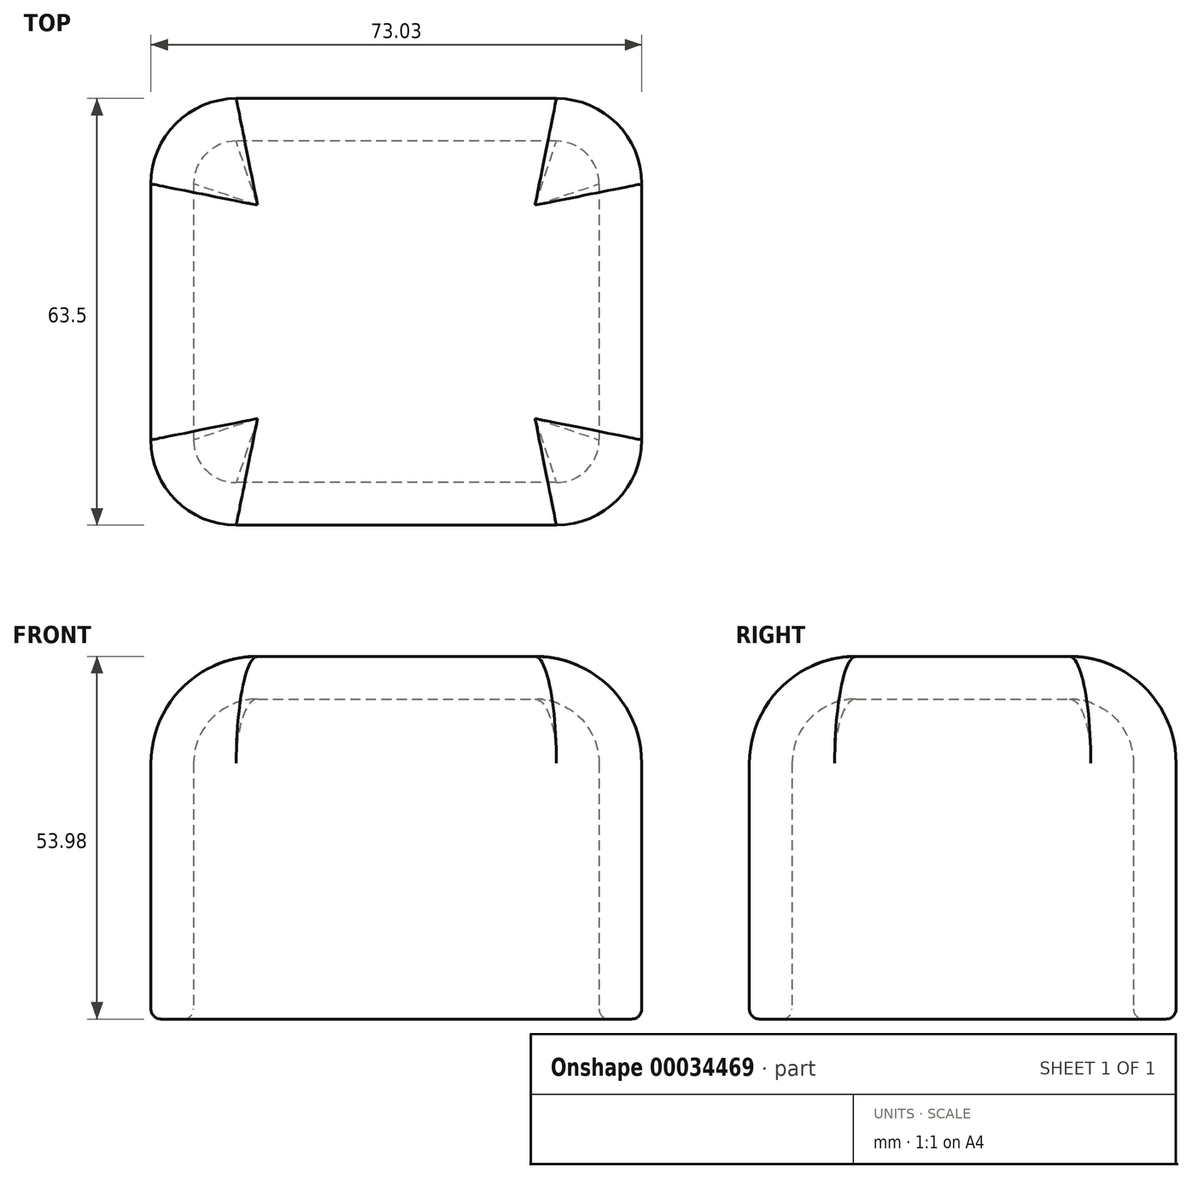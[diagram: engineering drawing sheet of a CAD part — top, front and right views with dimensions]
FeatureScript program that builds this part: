
annotation { "Feature Type Name" : "Feature", "Feature Type Description" : "" }
export const myFeature = defineFeature(function(context is Context, id is Id, definition is map)
    precondition{}
    {
        {
            var Q0;
            Q0=qCreatedBy(makeId("Top.planeOp"),FACE);
            var sketch = newSketch(context, id + "F4", { "sketchPlane" : qUnion([Q0])});
            skLineSegment(sketch, "E0.bottom", {"start": v(73.02, 63.5) * mm, "end": v(0, 63.5) * mm});
            skLineSegment(sketch, "E0.top", {"start": v(73.03, 0) * mm, "end": v(0, 0) * mm});
            skLineSegment(sketch, "E0.left", {"start": v(73.03, 63.5) * mm, "end": v(73.03, 0) * mm});
            skLineSegment(sketch, "E0.right", {"start": v(0, 63.5) * mm, "end": v(0, 0) * mm});
            skSolve(sketch);
        }
        {
            var Q0;
            Q0 = qSketchRegion(id + "F4", true);
            var sketch = newSketch(context, id + "F0", { "sketchPlane" : qUnion([Q0])});
            skSolve(sketch);
        }
        {
            var Q0;
            Q0 = qSketchRegion(id + "F0", true);
            var Q1;
            Q1=makeQuery(id+"F4.imprint","IMPRINT",FACE,{"disambiguationData":[TD([[makeQuery(id+"F4.imprint","IMPRINT",EDGE,{"derivedFrom":sQuery(id+"F4.wireOp",EDGE,"E0.bottom")}),1.0]])]});
            extrude(context, id + "F5", {"entities" : qUnion([Q0, Q1]), "depth" : 53.97 * mm});
        }
        {
            var Q0;
            Q0=makeQuery(id+"F5.opExtrude","SWEPT_EDGE",EDGE,{"disambiguationData":[OSD([sQuery(id+"F4.wireOp",EDGE,"E0.top"),sQuery(id+"F4.wireOp",EDGE,"E0.left")])]});
            var Q1;
            Q1=makeQuery(id+"F5.opExtrude","SWEPT_EDGE",EDGE,{"disambiguationData":[OSD([sQuery(id+"F4.wireOp",EDGE,"E0.bottom"),sQuery(id+"F4.wireOp",EDGE,"E0.left")])]});
            var Q2;
            Q2=makeQuery(id+"F5.opExtrude","SWEPT_EDGE",EDGE,{"disambiguationData":[OSD([sQuery(id+"F4.wireOp",EDGE,"E0.top"),sQuery(id+"F4.wireOp",EDGE,"E0.right")])]});
            var Q3;
            Q3=makeQuery(id+"F5.opExtrude","SWEPT_EDGE",EDGE,{"disambiguationData":[OSD([sQuery(id+"F4.wireOp",EDGE,"E0.bottom"),sQuery(id+"F4.wireOp",EDGE,"E0.right")])]});
            fillet(context, id + "F1", {"entities" : qUnion([Q0, Q1, Q2, Q3]), "radius" : 12.7 * mm, "tangentPropagation" : true, "allowEdgeOverflow" : false});
        }
        {
            var Q0;
            Q0=makeQuery(id+"F5.opExtrude","CAP_EDGE",EDGE,{"disambiguationData":[OSD([sQuery(id+"F4.wireOp",EDGE,"E0.right")])],"isStart":false});
            fillet(context, id + "F2", {"entities" : qUnion([Q0]), "radius" : 15.88 * mm, "tangentPropagation" : true, "allowEdgeOverflow" : false});
        }
        {
            var Q0;
            Q0=makeQuery(id+"F5.opExtrude","CAP_FACE",FACE,{"disambiguationData":[OSD([sQuery(id+"F4.wireOp",EDGE,"E0.bottom"),sQuery(id+"F4.wireOp",EDGE,"E0.top"),sQuery(id+"F4.wireOp",EDGE,"E0.left"),sQuery(id+"F4.wireOp",EDGE,"E0.right")])],"isStart":true});
            shell(context, id + "F3", {"entities" : qUnion([Q0]), "thickness" : 6.35 * mm});
        }
        {
            var Q0;
            Q0=makeQuery(id+"F5.opExtrude","CAP_FACE",FACE,{"disambiguationData":[OSD([sQuery(id+"F4.wireOp",EDGE,"E0.bottom"),sQuery(id+"F4.wireOp",EDGE,"E0.top"),sQuery(id+"F4.wireOp",EDGE,"E0.left"),sQuery(id+"F4.wireOp",EDGE,"E0.right")])],"isStart":true});
            fillet(context, id + "F6", {"entities" : qUnion([Q0]), "radius" : 1.52 * mm, "tangentPropagation" : true, "allowEdgeOverflow" : false});
        }
    });
